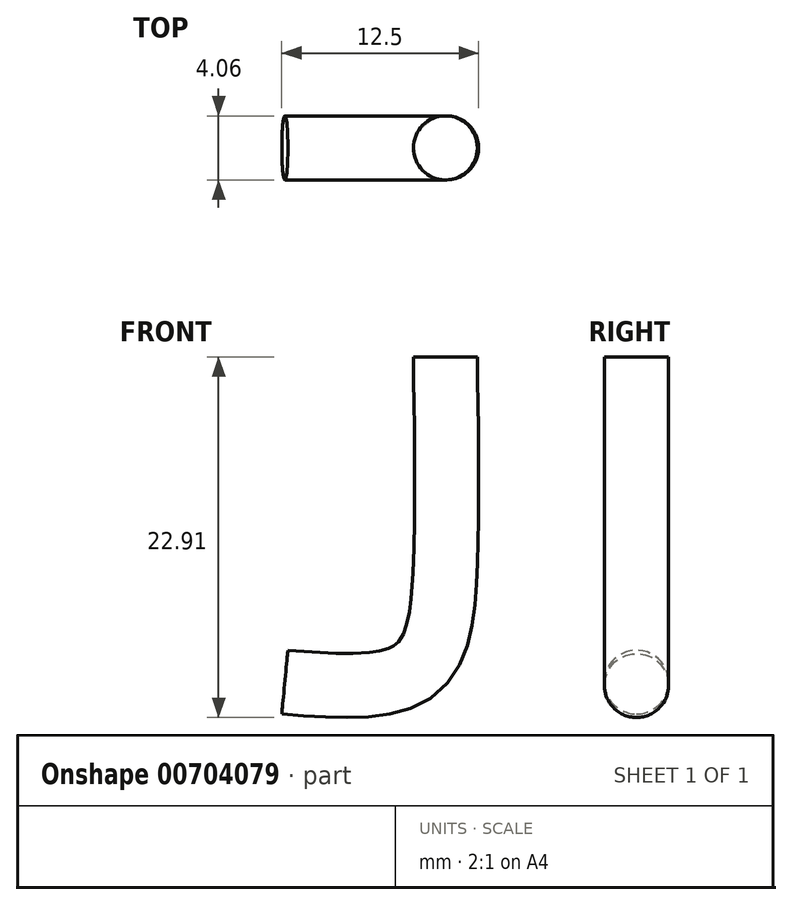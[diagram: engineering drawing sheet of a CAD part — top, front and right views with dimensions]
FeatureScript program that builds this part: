
annotation { "Feature Type Name" : "Feature", "Feature Type Description" : "" }
export const myFeature = defineFeature(function(context is Context, id is Id, definition is map)
    precondition{}
    {
        {
            var Q0;
            Q0=qCreatedBy(makeId("Front.planeOp"),FACE);
            var sketch = newSketch(context, id + "F0", { "sketchPlane" : qUnion([Q0])});
            skFitSpline(sketch, "E0", {"points": [v(0, 0) * mm, v(0, -13.14) * mm, v(-1.87, -19.84) * mm, v(-10.2, -20.66) * mm], "startDerivative": vector(0.53, -34.71) * mm, "endDerivative": vector(-31.45, 2.55) * mm});
            skSolve(sketch);
        }
        {
            var Q0;
            Q0=qCreatedBy(makeId("Top.planeOp"),FACE);
            var sketch = newSketch(context, id + "F1", { "sketchPlane" : qUnion([Q0])});
            skCircle(sketch, "E1", {"center": v(0, 0) * mm, "radius": 2.03 * mm});
            skSolve(sketch);
        }
        {
            var Q0;
            Q0=makeQuery(id+"F1.imprint","IMPRINT",FACE,{"disambiguationData":[TD([[makeQuery(id+"F1.imprint","IMPRINT",EDGE,{"derivedFrom":sQuery(id+"F1.wireOp",EDGE,"E1")}),1.0]])]});
            var Q1;
            Q1=sQuery(id+"F0.wireOp",EDGE,"E0");
            sweep(context, id + "F2", {"profiles" : qUnion([Q0]), "path" : qUnion([Q1])});
        }
    });
